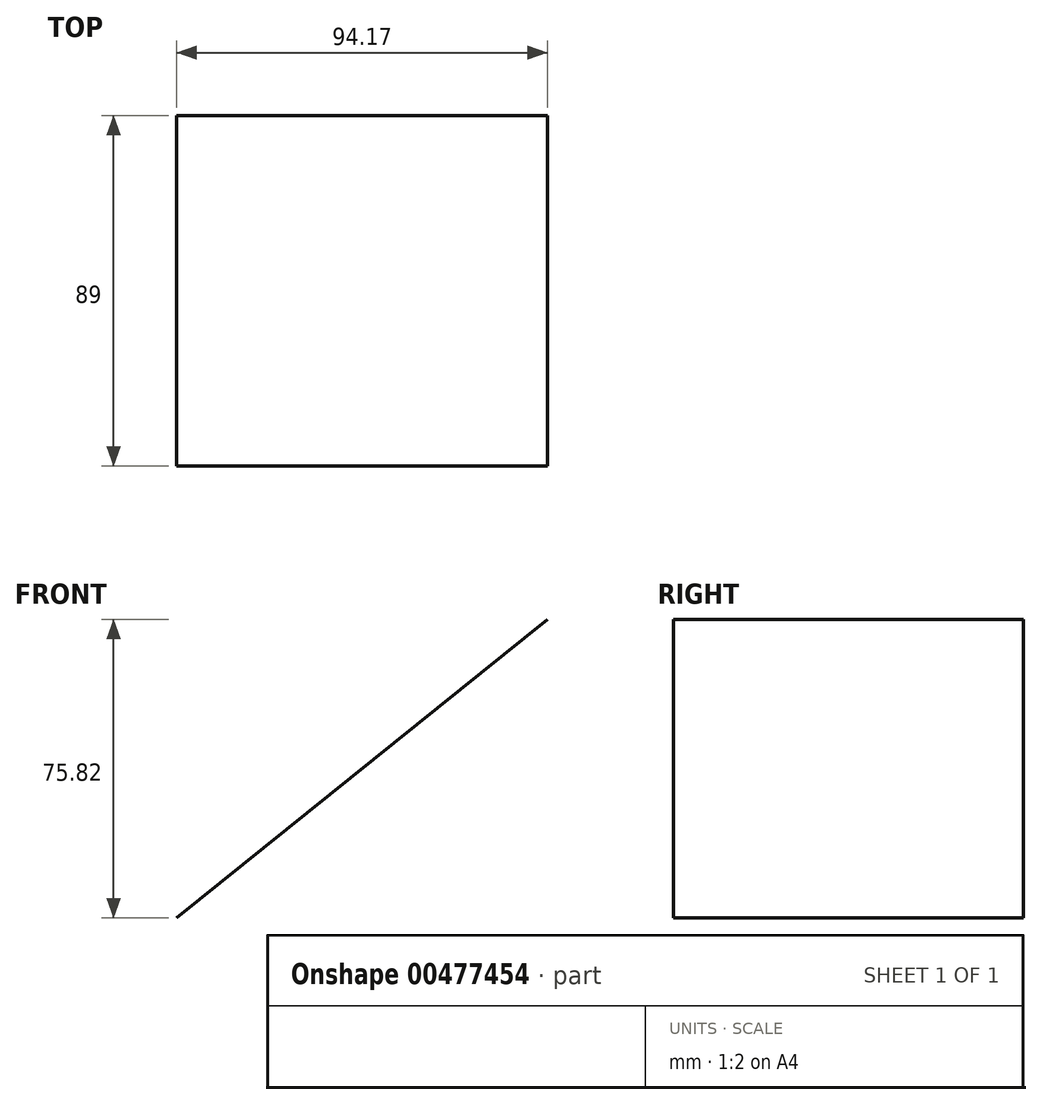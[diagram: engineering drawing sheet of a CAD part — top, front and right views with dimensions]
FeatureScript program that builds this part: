
annotation { "Feature Type Name" : "Feature", "Feature Type Description" : "" }
export const myFeature = defineFeature(function(context is Context, id is Id, definition is map)
    precondition{}
    {
        {
            var Q0;
            Q0=qCreatedBy(makeId("Front.planeOp"),FACE);
            var sketch = newSketch(context, id + "F0", { "sketchPlane" : qUnion([Q0])});
            skLineSegment(sketch, "E0", {"start": v(-123.35, -19.26) * mm, "end": v(-29.18, 56.56) * mm});
            skSolve(sketch);
        }
        {
            var Q0;
            Q0=sQuery(id+"F0.wireOp",EDGE,"E0");
            extrude(context, id + "F1", {"bodyType" : ToolBodyType.SURFACE, "surfaceEntities" : qUnion([Q0]), "depth" : 89 * mm});
        }
    });
